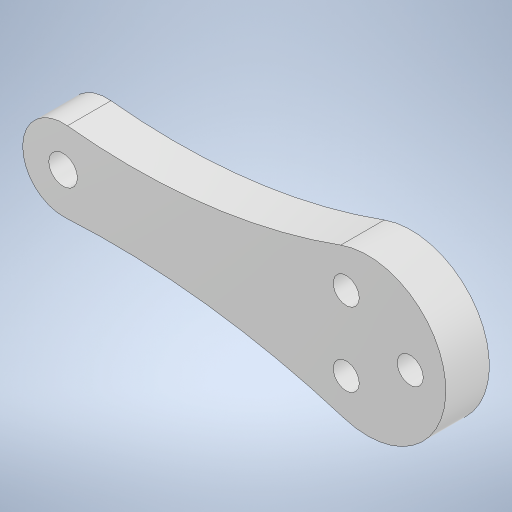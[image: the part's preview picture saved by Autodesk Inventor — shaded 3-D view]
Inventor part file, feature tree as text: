
AUTODESK INVENTOR PART (.ipt)
format: ipt  version: 2023 (Build 270158000, 158)  size: 233,984 bytes
history: native  units: mm
features: extrude x1, sketch x1
ambient origin geometry x8: Origin, YZ Plane, XZ Plane, XY Plane, X Axis, Y Axis, Z Axis, Center Point
bodies: Solid1 (feature_tree)
feature tree (2):
  extrude  "Extrusion1"  Depth=5.0mm TaperAngle=0.0deg
  sketch  "Sketch1"  dims[d1=30.0mm d2=35.0mm d3=3.3mm d4=3.0mm d5=3.0mm d6=360.0deg d7=5.5mm d8=18.0mm d9=70.0mm d10=90.0mm d11=5.0mm d12=0.0mm]
